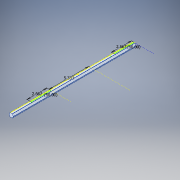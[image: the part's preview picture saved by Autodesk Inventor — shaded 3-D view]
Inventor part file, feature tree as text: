
AUTODESK INVENTOR PART (.ipt)
format: ipt  version: 2017 (Build 210142000, 142)  size: 149,504 bytes
history: native  units: in
note: dims shown in document units (in); Inventor stores cm internally (conversion verified against a paired STEP export)
features: sketch x5, split x1, fillet x1
ambient origin geometry x8: Origin, YZ Plane, XZ Plane, XY Plane, X Axis, Y Axis, Z Axis, Center Point
bodies: Solid1 (feature_tree)
feature tree (7):
  sketch  "Sketch1"  dims[d5=5.333in]
  split  "Split1"
  sketch  "Sketch3"  dims[d8=90.0deg]
  sketch  "Sketch4"  dims[d9=2.6665in]
  sketch  "Sketch5"  dims[d10=90.0deg d11=16.5in]
  sketch  "Sketch2"  dims[d7=2.6665in]
  fillet  "Fillet1"  Radius=8.5in
